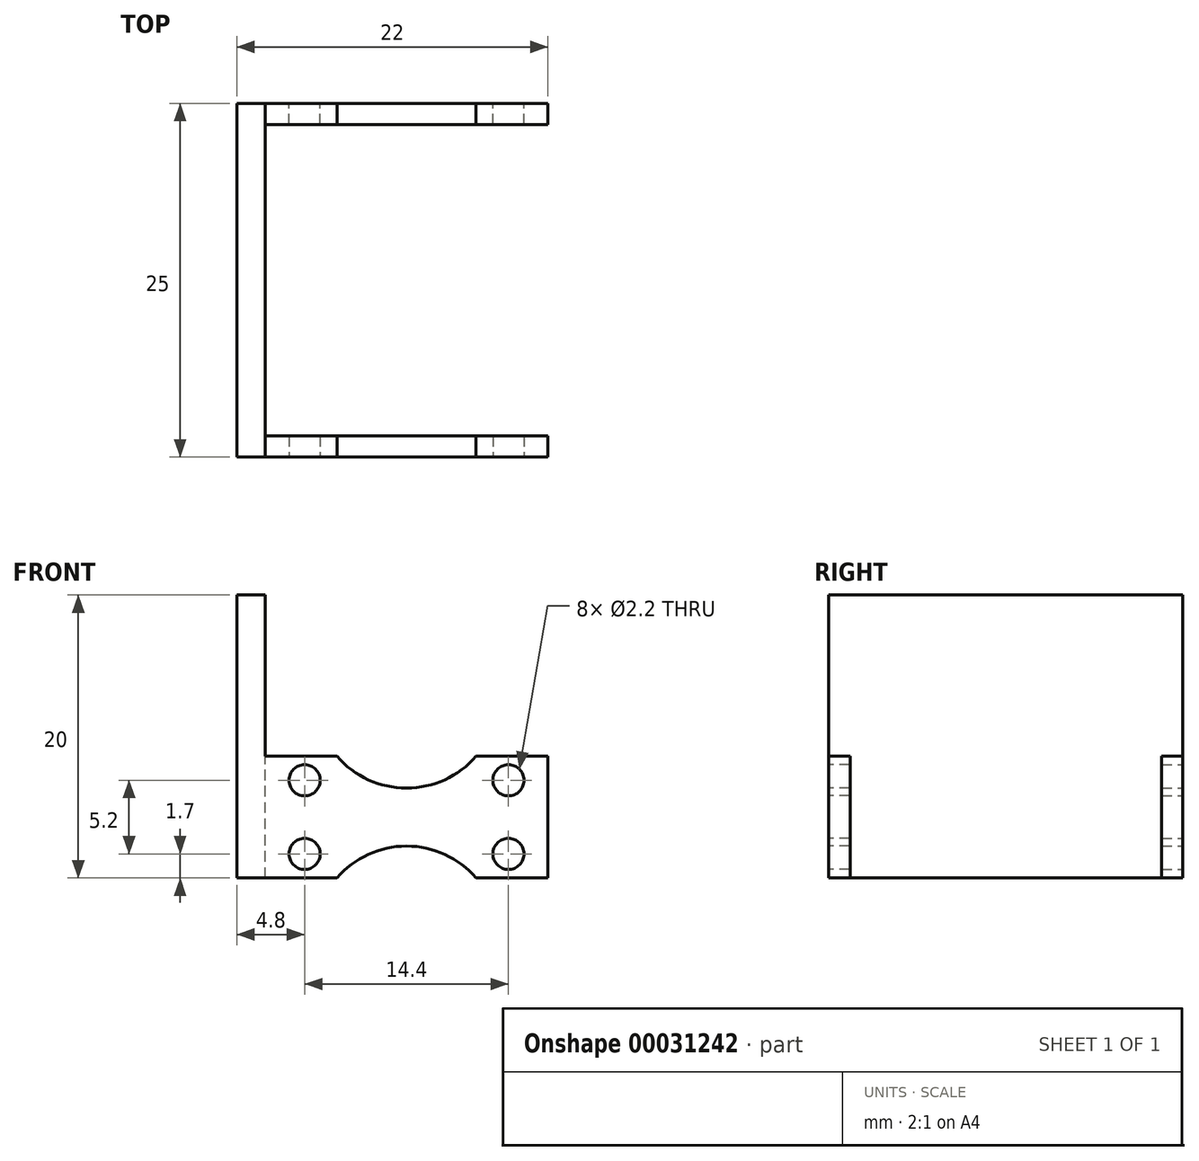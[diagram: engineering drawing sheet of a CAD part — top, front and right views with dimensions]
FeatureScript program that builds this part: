
annotation { "Feature Type Name" : "Feature", "Feature Type Description" : "" }
export const myFeature = defineFeature(function(context is Context, id is Id, definition is map)
    precondition{}
    {
        {
            var Q0;
            Q0=qCreatedBy(makeId("Front.planeOp"),FACE);
            var sketch = newSketch(context, id + "F0", { "sketchPlane" : qUnion([Q0])});
            skLineSegment(sketch, "E0.bottom", {"start": v(0, 0) * mm, "end": v(20, 0) * mm});
            skLineSegment(sketch, "E0.top", {"start": v(0, 8.6) * mm, "end": v(20, 8.6) * mm});
            skLineSegment(sketch, "E0.left", {"start": v(0, 0) * mm, "end": v(0, 8.6) * mm});
            skLineSegment(sketch, "E0.right", {"start": v(20, 0) * mm, "end": v(20, 8.6) * mm});
            skSolve(sketch);
        }
        {
            var Q0;
            Q0=qSketchRegion(id+"F0",true);
            extrude(context, id + "F1", {"entities" : qUnion([Q0]), "depth" : 1.5 * mm});
        }
        {
            var Q0;
            Q0=makeQuery(id+"F1.opExtrude","CAP_FACE",FACE,{"disambiguationData":[OSD([sQuery(id+"F0.wireOp",EDGE,"E0.bottom"),sQuery(id+"F0.wireOp",EDGE,"E0.top"),sQuery(id+"F0.wireOp",EDGE,"E0.left"),sQuery(id+"F0.wireOp",EDGE,"E0.right")])],"isStart":false});
            var sketch = newSketch(context, id + "F2", { "sketchPlane" : qUnion([Q0])});
            skLineSegment(sketch, "E1", {"start": v(0, 4.3) * mm, "end": v(20, 4.3) * mm, "construction": true});
            skLineSegment(sketch, "E2", {"start": v(10, 8.6) * mm, "end": v(10, 0) * mm, "construction": true});
            skPoint(sketch, "E3", {"position": v(10, 4.3) * mm});
            skCircle(sketch, "E4", {"center": v(2.8, 6.9) * mm, "radius": 1.1 * mm});
            skCircle(sketch, "E5.MirrorC", {"center": v(17.2, 6.9) * mm, "radius": 1.1 * mm});
            skCircle(sketch, "E6.MirrorC", {"center": v(2.8, 1.7) * mm, "radius": 1.1 * mm});
            skCircle(sketch, "E7.MirrorC", {"center": v(17.2, 1.7) * mm, "radius": 1.1 * mm});
            skLineSegment(sketch, "E8", {"start": v(0, 12.85) * mm, "end": v(19.96, 12.85) * mm, "construction": true});
            skPoint(sketch, "E9", {"position": v(10, 12.85) * mm});
            skArc(sketch, "E10", {"start": v(5.08, 8.6) * mm, "mid": v(10, 6.35) * mm, "end": v(14.92, 8.6) * mm});
            skLineSegment(sketch, "E11", {"start": v(5.08, 8.6) * mm, "end": v(14.92, 8.6) * mm});
            skArc(sketch, "E12.MirrorCS", {"start": v(5.08, 0) * mm, "mid": v(10, 2.25) * mm, "end": v(14.92, 0) * mm});
            skLineSegment(sketch, "E13.MirrorCS", {"start": v(5.08, 0) * mm, "end": v(14.92, 0) * mm});
            skSolve(sketch);
        }
        {
            var Q0;
            Q0=qSketchRegion(id+"F2",true);
            extrude(context, id + "F3", {"entities" : qUnion([Q0]), "operationType" : NewBodyOperationType.REMOVE, "endBound" : BoundingType.UP_TO_NEXT, "oppositeDirection" : true, "depth" : 25 * mm});
        }
        {
            var Q0;
            Q0=makeQuery(id+"F1.opExtrude","CAP_FACE",FACE,{"disambiguationData":[OSD([sQuery(id+"F0.wireOp",EDGE,"E0.bottom"),sQuery(id+"F0.wireOp",EDGE,"E0.top"),sQuery(id+"F0.wireOp",EDGE,"E0.left"),sQuery(id+"F0.wireOp",EDGE,"E0.right")])],"isStart":false});
            var sketch = newSketch(context, id + "F4", { "sketchPlane" : qUnion([Q0])});
            skLineSegment(sketch, "E14.bottom", {"start": v(0, 0) * mm, "end": v(-2, 0) * mm});
            skLineSegment(sketch, "E14.top", {"start": v(0, 20) * mm, "end": v(-2, 20) * mm});
            skLineSegment(sketch, "E14.left", {"start": v(0, 0) * mm, "end": v(0, 20) * mm});
            skLineSegment(sketch, "E14.right", {"start": v(-2, 0) * mm, "end": v(-2, 20) * mm});
            skSolve(sketch);
        }
        {
            var Q0;
            Q0 = qSketchRegion(id + "F4", true);
            extrude(context, id + "F5", {"entities" : qUnion([Q0]), "operationType" : NewBodyOperationType.ADD, "oppositeDirection" : true, "depth" : 12.5 * mm});
        }
        {
            var Q0;
            Q0=qCreatedBy(makeId("Front.planeOp"),FACE);
            cPlane(context, id + "F6", {"entities" : qUnion([Q0]), "cplaneType" : CPlaneType.OFFSET, "offset" : 11 * mm, "oppositeDirection" : true, "width" : 150 * mm, "height" : 150 * mm});
        }
        {
            var Q0;
            Q0=makeQuery(id+"F1.opExtrude","SWEPT_BODY",BODY,{"disambiguationData":[OSD([sQuery(id+"F0.wireOp",EDGE,"E0.bottom"),sQuery(id+"F0.wireOp",EDGE,"E0.top"),sQuery(id+"F0.wireOp",EDGE,"E0.left"),sQuery(id+"F0.wireOp",EDGE,"E0.right")])]});
            var Q1;
            Q1=qCreatedBy(id+"F6.planeOp",FACE);
            mirror(context, id + "F7", {"operationType" : NewBodyOperationType.ADD, "entities" : qUnion([Q0]), "mirrorPlane" : qUnion([Q1])});
        }
    });
